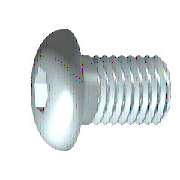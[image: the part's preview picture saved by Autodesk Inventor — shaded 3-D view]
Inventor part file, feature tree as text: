
AUTODESK INVENTOR PART (.ipt)
format: ipt  version: 2021 (Build 250183000, 183)  size: 209,920 bytes
history: native  units: mm (DEFAULTED — no unit token found)
features: sketch x2, extrude x1, plane x1, fillet x1
ambient origin geometry x7: Origin, YZ Plane, XY Plane, X Axis, Y Axis, Z Axis, Center Point
bodies: Solid1 (feature_tree), Body (feature_tree)
feature tree (5):
  extrude  "Slot"  Depth=1.65mm
  plane  "Work Plane1"
  fillet  "Fillet2"  Radius=1.65mm
  sketch  "Sketch1"  dims[d1=4.5mm d2=0.306825mm d3=1.65mm]
  sketch  "Sketch2"  dims[d4=1.04mm d5=60.0deg d6=3.0mm d7=3.0mm d8=2.309401mm d9=5.7mm d10=90.0deg d11=10.0mm d12=0.0mm d13=4.5mm d14=0.0mm d15=0.306725mm d16=0.306725mm d17=1.45mm d19=0.0mm d26=6.0mm d27=45.0deg d28=0.0mm d29=0.0mm d30=0.3mm]
